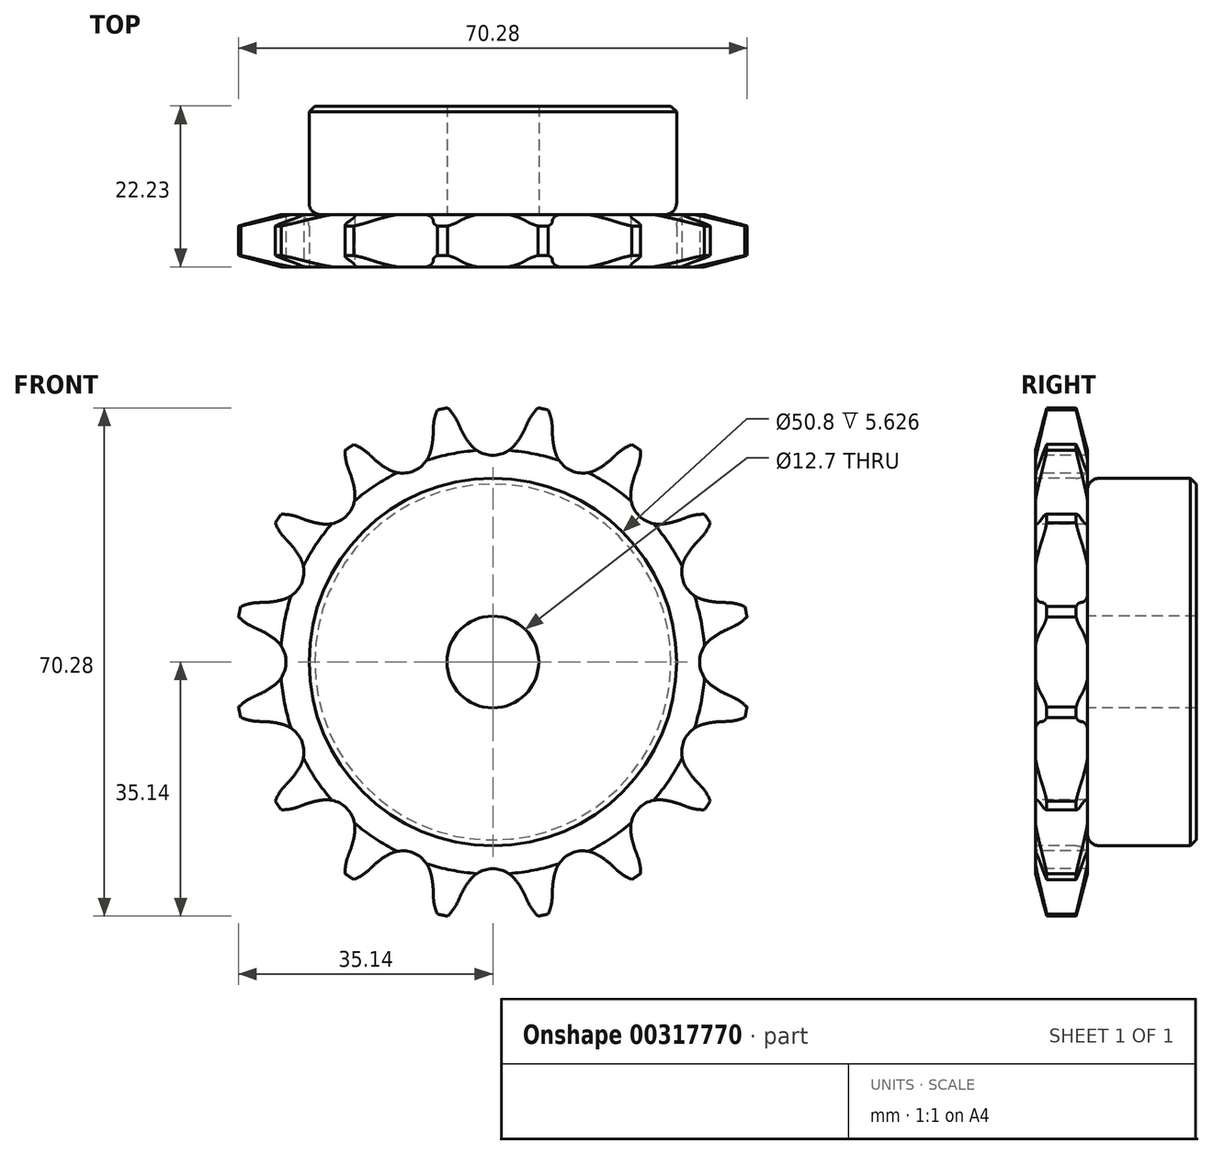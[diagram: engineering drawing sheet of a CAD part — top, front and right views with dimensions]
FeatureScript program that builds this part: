
annotation { "Feature Type Name" : "Feature", "Feature Type Description" : "" }
export const myFeature = defineFeature(function(context is Context, id is Id, definition is map)
    precondition{}
    {
        {
            var Q0;
            Q0=qCreatedBy(makeId("Right.planeOp"),FACE);
            var sketch = newSketch(context, id + "F0", { "sketchPlane" : qUnion([Q0])});
            skLineSegment(sketch, "E0", {"start": v(0, 0) * mm, "end": v(22.23, 0) * mm});
            skLineSegment(sketch, "E1.bottom", {"start": v(0, 6.35) * mm, "end": v(7.21, 6.35) * mm});
            skLineSegment(sketch, "E1.top", {"start": v(0, 35.69) * mm, "end": v(7.21, 35.69) * mm});
            skLineSegment(sketch, "E1.left", {"start": v(0, 6.35) * mm, "end": v(0, 35.69) * mm});
            skLineSegment(sketch, "E1.right", {"start": v(7.21, 6.35) * mm, "end": v(7.21, 35.69) * mm});
            skLineSegment(sketch, "E2.bottom", {"start": v(0, 6.35) * mm, "end": v(22.23, 6.35) * mm});
            skLineSegment(sketch, "E2.top", {"start": v(0, 25.4) * mm, "end": v(22.23, 25.4) * mm});
            skLineSegment(sketch, "E2.left", {"start": v(0, 6.35) * mm, "end": v(0, 25.4) * mm});
            skLineSegment(sketch, "E2.right", {"start": v(22.23, 6.35) * mm, "end": v(22.22, 25.4) * mm});
            skLineSegment(sketch, "E3.MirrorCS", {"start": v(0, -6.35) * mm, "end": v(7.21, -6.35) * mm});
            skLineSegment(sketch, "E4.MirrorCS", {"start": v(0, -25.4) * mm, "end": v(22.23, -25.4) * mm});
            skLineSegment(sketch, "E5.MirrorCS", {"start": v(0, -6.35) * mm, "end": v(22.23, -6.35) * mm});
            skLineSegment(sketch, "E6.MirrorCS", {"start": v(22.23, -6.35) * mm, "end": v(22.23, -25.4) * mm});
            skLineSegment(sketch, "E7.MirrorCS", {"start": v(7.21, -6.35) * mm, "end": v(7.21, -35.69) * mm});
            skLineSegment(sketch, "E8.MirrorCS", {"start": v(0, -6.35) * mm, "end": v(0, -35.69) * mm});
            skLineSegment(sketch, "E9.MirrorCS", {"start": v(0, -35.69) * mm, "end": v(7.21, -35.69) * mm});
            skLineSegment(sketch, "E10.MirrorCS", {"start": v(0, -6.35) * mm, "end": v(0, -25.4) * mm});
            skSolve(sketch);
        }
        {
            var Q0;
            {var subQ5=sQuery(id+"F0.wireOp",EDGE,"E2.right");Q0=makeQuery(id+"F0.imprint","IMPRINT",FACE,{"disambiguationData":[TD([[makeQuery(id+"F0.imprint","IMPRINT",EDGE,{"derivedFrom":subQ5}),1.0]])]});}
            var Q1;
            {var subQ5=sQuery(id+"F0.wireOp",EDGE,"E2.left");Q1=makeQuery(id+"F0.imprint","IMPRINT",FACE,{"disambiguationData":[TD([[makeQuery(id+"F0.imprint","IMPRINT",EDGE,{"derivedFrom":subQ5}),-1.0]])]});}
            var Q2;
            {var subQ0=sQuery(id+"F0.wireOp",EDGE,"E1.top");Q2=makeQuery(id+"F0.imprint","IMPRINT",FACE,{"disambiguationData":[TD([[makeQuery(id+"F0.imprint","IMPRINT",EDGE,{"derivedFrom":subQ0}),-1.0]])]});}
            var Q3;
            Q3=sQuery(id+"F0.wireOp",EDGE,"E0");
            revolve(context, id + "F1", {"entities" : qUnion([Q0, Q1, Q2]), "axis" : qUnion([Q3]), "revolveType" : RevolveType.FULL});
        }
        {
            var Q0;
            Q0=makeQuery(id+"F1.opRevolve","SWEPT_EDGE",EDGE,{"disambiguationData":[OSD([sQuery(id+"F0.wireOp",EDGE,"E1.right"),sQuery(id+"F0.wireOp",EDGE,"E2.top")])]});
            fillet(context, id + "F2", {"entities" : qUnion([Q0]), "radius" : 1.59 * mm, "tangentPropagation" : true, "allowEdgeOverflow" : false});
        }
        {
            var Q0;
            Q0=makeQuery(id+"F1.opRevolve","SWEPT_EDGE",EDGE,{"disambiguationData":[OSD([sQuery(id+"F0.wireOp",EDGE,"E2.top"),sQuery(id+"F0.wireOp",EDGE,"E2.right")])]});
            chamfer(context, id + "F3", {"entities" : qUnion([Q0]), "width" : 0.8 * mm, "tangentPropagation" : true});
        }
        {
            var Q0;
            Q0=makeQuery(id+"F1.opRevolve","SWEPT_EDGE",EDGE,{"disambiguationData":[OSD([sQuery(id+"F0.wireOp",EDGE,"E1.top"),sQuery(id+"F0.wireOp",EDGE,"E1.left")])]});
            var Q1;
            Q1=makeQuery(id+"F1.opRevolve","SWEPT_EDGE",EDGE,{"disambiguationData":[OSD([sQuery(id+"F0.wireOp",EDGE,"E1.top"),sQuery(id+"F0.wireOp",EDGE,"E1.right")])]});
            chamfer(context, id + "F4", {"entities" : qUnion([Q0, Q1]), "chamferType" : ChamferType.TWO_OFFSETS, "width1" : 6.35 * mm, "oppositeDirection" : false, "width2" : 1.57 * mm, "tangentPropagation" : true});
        }
        {
            var Q0;
            Q0=makeQuery(id+"F1.opRevolve","SWEPT_FACE",FACE,{"disambiguationData":[OSD([sQuery(id+"F0.wireOp",EDGE,"E1.left"),sQuery(id+"F0.wireOp",EDGE,"E2.left")])]});
            var sketch = newSketch(context, id + "F5", { "sketchPlane" : qUnion([Q0])});
            skCircle(sketch, "E11", {"center": v(0, 0) * mm, "radius": 32.55 * mm, "construction": true});
            skLineSegment(sketch, "E12", {"start": v(0, 0) * mm, "end": v(0, 32.55) * mm, "construction": true});
            skLineSegment(sketch, "E13", {"start": v(47.22, 32.55) * mm, "end": v(0, 32.55) * mm, "construction": true});
            skLineSegment(sketch, "E14", {"start": v(0, 32.55) * mm, "end": v(5, 36.56) * mm, "construction": true});
            skLineSegment(sketch, "E15", {"start": v(5, 36.56) * mm, "end": v(-4.46, 32.3) * mm, "construction": true});
            skLineSegment(sketch, "E16", {"start": v(-4.46, 32.3) * mm, "end": v(-4.82, 33.1) * mm});
            skLineSegment(sketch, "E17", {"start": v(0, 0) * mm, "end": v(-7.13, 35.85) * mm, "construction": true});
            skArc(sketch, "E18", {"start": v(-7.13, 35.85) * mm, "mid": v(-15.87, 26.15) * mm, "end": v(-4.82, 33.1) * mm, "construction": true});
            skArc(sketch, "E19", {"start": v(-4.82, 33.1) * mm, "mid": v(-5.78, 34.63) * mm, "end": v(-7.13, 35.85) * mm});
            skLineSegment(sketch, "E20", {"start": v(-4.82, 33.1) * mm, "end": v(-4.82, 33.1) * mm});
            skLineSegment(sketch, "E21", {"start": v(-4.46, 32.3) * mm, "end": v(-4.46, 32.3) * mm});
            skArc(sketch, "E22", {"start": v(-3.1, 30.07) * mm, "mid": v(13.83, 41.97) * mm, "end": v(-4.46, 32.3) * mm, "construction": true});
            skArc(sketch, "E23.MirrorCS", {"start": v(4.82, 33.1) * mm, "mid": v(5.78, 34.63) * mm, "end": v(7.13, 35.85) * mm});
            skArc(sketch, "E24.MirrorCS", {"start": v(4.46, 32.3) * mm, "mid": v(3.84, 31.14) * mm, "end": v(3.1, 30.07) * mm});
            skArc(sketch, "E25", {"start": v(-4.46, 32.3) * mm, "mid": v(-3.84, 31.14) * mm, "end": v(-3.1, 30.07) * mm});
            skLineSegment(sketch, "E26", {"start": v(-4.82, 33.1) * mm, "end": v(-11.63, 48.22) * mm, "construction": true});
            skLineSegment(sketch, "E27.MirrorCS", {"start": v(4.46, 32.3) * mm, "end": v(4.82, 33.1) * mm});
            skArc(sketch, "E28", {"start": v(3.1, 30.07) * mm, "mid": v(0, 36.51) * mm, "end": v(-3.1, 30.07) * mm, "construction": true});
            skArc(sketch, "E29", {"start": v(-3.1, 30.07) * mm, "mid": v(0, 28.59) * mm, "end": v(3.1, 30.07) * mm});
            skLineSegment(sketch, "E30.1.0", {"start": v(-16.48, 28.14) * mm, "end": v(-17.12, 28.74) * mm});
            skArc(sketch, "E30.1.1", {"start": v(-17.12, 28.74) * mm, "mid": v(-18.6, 29.79) * mm, "end": v(-20.3, 30.4) * mm});
            skArc(sketch, "E30.1.2", {"start": v(-14.36, 26.6) * mm, "mid": v(-10.94, 26.41) * mm, "end": v(-8.65, 28.96) * mm});
            skArc(sketch, "E30.1.3", {"start": v(-16.48, 28.14) * mm, "mid": v(-15.47, 27.3) * mm, "end": v(-14.36, 26.6) * mm});
            skArc(sketch, "E30.1.4", {"start": v(-8.24, 31.55) * mm, "mid": v(-8.37, 30.24) * mm, "end": v(-8.65, 28.96) * mm});
            skLineSegment(sketch, "E30.1.5", {"start": v(-8.24, 31.55) * mm, "end": v(-8.22, 32.42) * mm});
            skArc(sketch, "E30.1.6", {"start": v(-8.22, 32.42) * mm, "mid": v(-7.91, 34.21) * mm, "end": v(-7.13, 35.85) * mm});
            skLineSegment(sketch, "E30.2.0", {"start": v(-26, 19.69) * mm, "end": v(-26.8, 20) * mm});
            skArc(sketch, "E30.2.1", {"start": v(-26.8, 20) * mm, "mid": v(-28.58, 20.4) * mm, "end": v(-30.4, 20.3) * mm});
            skArc(sketch, "E30.2.2", {"start": v(-23.45, 19.08) * mm, "mid": v(-20.21, 20.21) * mm, "end": v(-19.08, 23.45) * mm});
            skArc(sketch, "E30.2.3", {"start": v(-26, 19.69) * mm, "mid": v(-24.74, 19.3) * mm, "end": v(-23.45, 19.08) * mm});
            skArc(sketch, "E30.2.4", {"start": v(-19.69, 26) * mm, "mid": v(-19.3, 24.74) * mm, "end": v(-19.08, 23.45) * mm});
            skLineSegment(sketch, "E30.2.5", {"start": v(-19.69, 26) * mm, "end": v(-20, 26.8) * mm});
            skArc(sketch, "E30.2.6", {"start": v(-20, 26.8) * mm, "mid": v(-20.4, 28.58) * mm, "end": v(-20.3, 30.4) * mm});
            skLineSegment(sketch, "E30.3.0", {"start": v(-31.55, 8.24) * mm, "end": v(-32.42, 8.22) * mm});
            skArc(sketch, "E30.3.1", {"start": v(-32.42, 8.22) * mm, "mid": v(-34.21, 7.91) * mm, "end": v(-35.85, 7.13) * mm});
            skArc(sketch, "E30.3.2", {"start": v(-28.96, 8.65) * mm, "mid": v(-26.41, 10.94) * mm, "end": v(-26.6, 14.36) * mm});
            skArc(sketch, "E30.3.3", {"start": v(-31.55, 8.24) * mm, "mid": v(-30.24, 8.37) * mm, "end": v(-28.96, 8.65) * mm});
            skArc(sketch, "E30.3.4", {"start": v(-28.14, 16.48) * mm, "mid": v(-27.3, 15.47) * mm, "end": v(-26.6, 14.36) * mm});
            skLineSegment(sketch, "E30.3.5", {"start": v(-28.14, 16.48) * mm, "end": v(-28.74, 17.12) * mm});
            skArc(sketch, "E30.3.6", {"start": v(-28.74, 17.12) * mm, "mid": v(-29.79, 18.6) * mm, "end": v(-30.4, 20.3) * mm});
            skLineSegment(sketch, "E30.4.0", {"start": v(-32.3, -4.46) * mm, "end": v(-33.1, -4.82) * mm});
            skArc(sketch, "E30.4.1", {"start": v(-33.1, -4.82) * mm, "mid": v(-34.63, -5.78) * mm, "end": v(-35.85, -7.13) * mm});
            skArc(sketch, "E30.4.2", {"start": v(-30.07, -3.1) * mm, "mid": v(-28.59, 0) * mm, "end": v(-30.07, 3.1) * mm});
            skArc(sketch, "E30.4.3", {"start": v(-32.3, -4.46) * mm, "mid": v(-31.14, -3.84) * mm, "end": v(-30.07, -3.1) * mm});
            skArc(sketch, "E30.4.4", {"start": v(-32.3, 4.46) * mm, "mid": v(-31.14, 3.84) * mm, "end": v(-30.07, 3.1) * mm});
            skLineSegment(sketch, "E30.4.5", {"start": v(-32.3, 4.46) * mm, "end": v(-33.1, 4.82) * mm});
            skArc(sketch, "E30.4.6", {"start": v(-33.1, 4.82) * mm, "mid": v(-34.63, 5.78) * mm, "end": v(-35.85, 7.13) * mm});
            skLineSegment(sketch, "E30.5.0", {"start": v(-28.14, -16.48) * mm, "end": v(-28.74, -17.12) * mm});
            skArc(sketch, "E30.5.1", {"start": v(-28.74, -17.12) * mm, "mid": v(-29.79, -18.6) * mm, "end": v(-30.4, -20.3) * mm});
            skArc(sketch, "E30.5.2", {"start": v(-26.6, -14.36) * mm, "mid": v(-26.41, -10.94) * mm, "end": v(-28.96, -8.65) * mm});
            skArc(sketch, "E30.5.3", {"start": v(-28.14, -16.48) * mm, "mid": v(-27.3, -15.47) * mm, "end": v(-26.6, -14.36) * mm});
            skArc(sketch, "E30.5.4", {"start": v(-31.55, -8.24) * mm, "mid": v(-30.24, -8.37) * mm, "end": v(-28.96, -8.65) * mm});
            skLineSegment(sketch, "E30.5.5", {"start": v(-31.55, -8.24) * mm, "end": v(-32.42, -8.22) * mm});
            skArc(sketch, "E30.5.6", {"start": v(-32.42, -8.22) * mm, "mid": v(-34.21, -7.91) * mm, "end": v(-35.85, -7.13) * mm});
            skLineSegment(sketch, "E30.6.0", {"start": v(-19.69, -26) * mm, "end": v(-20, -26.8) * mm});
            skArc(sketch, "E30.6.1", {"start": v(-20, -26.8) * mm, "mid": v(-20.4, -28.58) * mm, "end": v(-20.3, -30.4) * mm});
            skArc(sketch, "E30.6.2", {"start": v(-19.08, -23.45) * mm, "mid": v(-20.21, -20.21) * mm, "end": v(-23.45, -19.08) * mm});
            skArc(sketch, "E30.6.3", {"start": v(-19.69, -26) * mm, "mid": v(-19.3, -24.74) * mm, "end": v(-19.08, -23.45) * mm});
            skArc(sketch, "E30.6.4", {"start": v(-26, -19.69) * mm, "mid": v(-24.74, -19.3) * mm, "end": v(-23.45, -19.08) * mm});
            skLineSegment(sketch, "E30.6.5", {"start": v(-26, -19.69) * mm, "end": v(-26.8, -20) * mm});
            skArc(sketch, "E30.6.6", {"start": v(-26.8, -20) * mm, "mid": v(-28.58, -20.4) * mm, "end": v(-30.4, -20.3) * mm});
            skLineSegment(sketch, "E30.7.0", {"start": v(-8.24, -31.55) * mm, "end": v(-8.22, -32.42) * mm});
            skArc(sketch, "E30.7.1", {"start": v(-8.22, -32.42) * mm, "mid": v(-7.91, -34.21) * mm, "end": v(-7.13, -35.85) * mm});
            skArc(sketch, "E30.7.2", {"start": v(-8.65, -28.96) * mm, "mid": v(-10.94, -26.41) * mm, "end": v(-14.36, -26.6) * mm});
            skArc(sketch, "E30.7.3", {"start": v(-8.24, -31.55) * mm, "mid": v(-8.37, -30.24) * mm, "end": v(-8.65, -28.96) * mm});
            skArc(sketch, "E30.7.4", {"start": v(-16.48, -28.14) * mm, "mid": v(-15.47, -27.3) * mm, "end": v(-14.36, -26.6) * mm});
            skLineSegment(sketch, "E30.7.5", {"start": v(-16.48, -28.14) * mm, "end": v(-17.12, -28.74) * mm});
            skArc(sketch, "E30.7.6", {"start": v(-17.12, -28.74) * mm, "mid": v(-18.6, -29.79) * mm, "end": v(-20.3, -30.4) * mm});
            skLineSegment(sketch, "E30.8.0", {"start": v(4.46, -32.3) * mm, "end": v(4.82, -33.1) * mm});
            skArc(sketch, "E30.8.1", {"start": v(4.82, -33.1) * mm, "mid": v(5.78, -34.63) * mm, "end": v(7.13, -35.85) * mm});
            skArc(sketch, "E30.8.2", {"start": v(3.1, -30.07) * mm, "mid": v(0, -28.59) * mm, "end": v(-3.1, -30.07) * mm});
            skArc(sketch, "E30.8.3", {"start": v(4.46, -32.3) * mm, "mid": v(3.84, -31.14) * mm, "end": v(3.1, -30.07) * mm});
            skArc(sketch, "E30.8.4", {"start": v(-4.46, -32.3) * mm, "mid": v(-3.84, -31.14) * mm, "end": v(-3.1, -30.07) * mm});
            skLineSegment(sketch, "E30.8.5", {"start": v(-4.46, -32.3) * mm, "end": v(-4.82, -33.1) * mm});
            skArc(sketch, "E30.8.6", {"start": v(-4.82, -33.1) * mm, "mid": v(-5.78, -34.63) * mm, "end": v(-7.13, -35.85) * mm});
            skLineSegment(sketch, "E30.9.0", {"start": v(16.48, -28.14) * mm, "end": v(17.12, -28.74) * mm});
            skArc(sketch, "E30.9.1", {"start": v(17.12, -28.74) * mm, "mid": v(18.6, -29.79) * mm, "end": v(20.3, -30.4) * mm});
            skArc(sketch, "E30.9.2", {"start": v(14.36, -26.6) * mm, "mid": v(10.94, -26.41) * mm, "end": v(8.65, -28.96) * mm});
            skArc(sketch, "E30.9.3", {"start": v(16.48, -28.14) * mm, "mid": v(15.47, -27.3) * mm, "end": v(14.36, -26.6) * mm});
            skArc(sketch, "E30.9.4", {"start": v(8.24, -31.55) * mm, "mid": v(8.37, -30.24) * mm, "end": v(8.65, -28.96) * mm});
            skLineSegment(sketch, "E30.9.5", {"start": v(8.24, -31.55) * mm, "end": v(8.22, -32.42) * mm});
            skArc(sketch, "E30.9.6", {"start": v(8.22, -32.42) * mm, "mid": v(7.91, -34.21) * mm, "end": v(7.13, -35.85) * mm});
            skLineSegment(sketch, "E30.10.0", {"start": v(26, -19.69) * mm, "end": v(26.8, -20) * mm});
            skArc(sketch, "E30.10.1", {"start": v(26.8, -20) * mm, "mid": v(28.58, -20.4) * mm, "end": v(30.4, -20.3) * mm});
            skArc(sketch, "E30.10.2", {"start": v(23.45, -19.08) * mm, "mid": v(20.21, -20.21) * mm, "end": v(19.08, -23.45) * mm});
            skArc(sketch, "E30.10.3", {"start": v(26, -19.69) * mm, "mid": v(24.74, -19.3) * mm, "end": v(23.45, -19.08) * mm});
            skArc(sketch, "E30.10.4", {"start": v(19.69, -26) * mm, "mid": v(19.3, -24.74) * mm, "end": v(19.08, -23.45) * mm});
            skLineSegment(sketch, "E30.10.5", {"start": v(19.69, -26) * mm, "end": v(20, -26.8) * mm});
            skArc(sketch, "E30.10.6", {"start": v(20, -26.8) * mm, "mid": v(20.4, -28.58) * mm, "end": v(20.3, -30.4) * mm});
            skLineSegment(sketch, "E30.11.0", {"start": v(31.55, -8.24) * mm, "end": v(32.42, -8.22) * mm});
            skArc(sketch, "E30.11.1", {"start": v(32.42, -8.22) * mm, "mid": v(34.21, -7.91) * mm, "end": v(35.85, -7.13) * mm});
            skArc(sketch, "E30.11.2", {"start": v(28.96, -8.65) * mm, "mid": v(26.41, -10.94) * mm, "end": v(26.6, -14.36) * mm});
            skArc(sketch, "E30.11.3", {"start": v(31.55, -8.24) * mm, "mid": v(30.24, -8.37) * mm, "end": v(28.96, -8.65) * mm});
            skArc(sketch, "E30.11.4", {"start": v(28.14, -16.48) * mm, "mid": v(27.3, -15.47) * mm, "end": v(26.6, -14.36) * mm});
            skLineSegment(sketch, "E30.11.5", {"start": v(28.14, -16.48) * mm, "end": v(28.74, -17.12) * mm});
            skArc(sketch, "E30.11.6", {"start": v(28.74, -17.12) * mm, "mid": v(29.79, -18.6) * mm, "end": v(30.4, -20.3) * mm});
            skLineSegment(sketch, "E30.12.0", {"start": v(32.3, 4.46) * mm, "end": v(33.1, 4.82) * mm});
            skArc(sketch, "E30.12.1", {"start": v(33.1, 4.82) * mm, "mid": v(34.63, 5.78) * mm, "end": v(35.85, 7.13) * mm});
            skArc(sketch, "E30.12.2", {"start": v(30.07, 3.1) * mm, "mid": v(28.59, 0) * mm, "end": v(30.07, -3.1) * mm});
            skArc(sketch, "E30.12.3", {"start": v(32.3, 4.46) * mm, "mid": v(31.14, 3.84) * mm, "end": v(30.07, 3.1) * mm});
            skArc(sketch, "E30.12.4", {"start": v(32.3, -4.46) * mm, "mid": v(31.14, -3.84) * mm, "end": v(30.07, -3.1) * mm});
            skLineSegment(sketch, "E30.12.5", {"start": v(32.3, -4.46) * mm, "end": v(33.1, -4.82) * mm});
            skArc(sketch, "E30.12.6", {"start": v(33.1, -4.82) * mm, "mid": v(34.63, -5.78) * mm, "end": v(35.85, -7.13) * mm});
            skLineSegment(sketch, "E30.13.0", {"start": v(28.14, 16.48) * mm, "end": v(28.74, 17.12) * mm});
            skArc(sketch, "E30.13.1", {"start": v(28.74, 17.12) * mm, "mid": v(29.79, 18.6) * mm, "end": v(30.4, 20.3) * mm});
            skArc(sketch, "E30.13.2", {"start": v(26.6, 14.36) * mm, "mid": v(26.41, 10.94) * mm, "end": v(28.96, 8.65) * mm});
            skArc(sketch, "E30.13.3", {"start": v(28.14, 16.48) * mm, "mid": v(27.3, 15.47) * mm, "end": v(26.6, 14.36) * mm});
            skArc(sketch, "E30.13.4", {"start": v(31.55, 8.24) * mm, "mid": v(30.24, 8.37) * mm, "end": v(28.96, 8.65) * mm});
            skLineSegment(sketch, "E30.13.5", {"start": v(31.55, 8.24) * mm, "end": v(32.42, 8.22) * mm});
            skArc(sketch, "E30.13.6", {"start": v(32.42, 8.22) * mm, "mid": v(34.21, 7.91) * mm, "end": v(35.85, 7.13) * mm});
            skLineSegment(sketch, "E30.14.0", {"start": v(19.69, 26) * mm, "end": v(20, 26.8) * mm});
            skArc(sketch, "E30.14.1", {"start": v(20, 26.8) * mm, "mid": v(20.4, 28.58) * mm, "end": v(20.3, 30.4) * mm});
            skArc(sketch, "E30.14.2", {"start": v(19.08, 23.45) * mm, "mid": v(20.21, 20.21) * mm, "end": v(23.45, 19.08) * mm});
            skArc(sketch, "E30.14.3", {"start": v(19.69, 26) * mm, "mid": v(19.3, 24.74) * mm, "end": v(19.08, 23.45) * mm});
            skArc(sketch, "E30.14.4", {"start": v(26, 19.69) * mm, "mid": v(24.74, 19.3) * mm, "end": v(23.45, 19.08) * mm});
            skLineSegment(sketch, "E30.14.5", {"start": v(26, 19.69) * mm, "end": v(26.8, 20) * mm});
            skArc(sketch, "E30.14.6", {"start": v(26.8, 20) * mm, "mid": v(28.58, 20.4) * mm, "end": v(30.4, 20.3) * mm});
            skLineSegment(sketch, "E30.15.0", {"start": v(8.24, 31.55) * mm, "end": v(8.22, 32.42) * mm});
            skArc(sketch, "E30.15.1", {"start": v(8.22, 32.42) * mm, "mid": v(7.91, 34.21) * mm, "end": v(7.13, 35.85) * mm});
            skArc(sketch, "E30.15.2", {"start": v(8.65, 28.96) * mm, "mid": v(10.94, 26.41) * mm, "end": v(14.36, 26.6) * mm});
            skArc(sketch, "E30.15.3", {"start": v(8.24, 31.55) * mm, "mid": v(8.37, 30.24) * mm, "end": v(8.65, 28.96) * mm});
            skArc(sketch, "E30.15.4", {"start": v(16.48, 28.14) * mm, "mid": v(15.47, 27.3) * mm, "end": v(14.36, 26.6) * mm});
            skLineSegment(sketch, "E30.15.5", {"start": v(16.48, 28.14) * mm, "end": v(17.12, 28.74) * mm});
            skArc(sketch, "E30.15.6", {"start": v(17.12, 28.74) * mm, "mid": v(18.6, 29.79) * mm, "end": v(20.3, 30.4) * mm});
            skSolve(sketch);
        }
        {
            var Q0;
            Q0 = qSketchRegion(id + "F5", true);
            extrude(context, id + "F6", {"entities" : qUnion([Q0]), "operationType" : NewBodyOperationType.INTERSECT, "endBound" : BoundingType.THROUGH_ALL, "oppositeDirection" : true, "depth" : 25.4 * mm});
        }
    });
